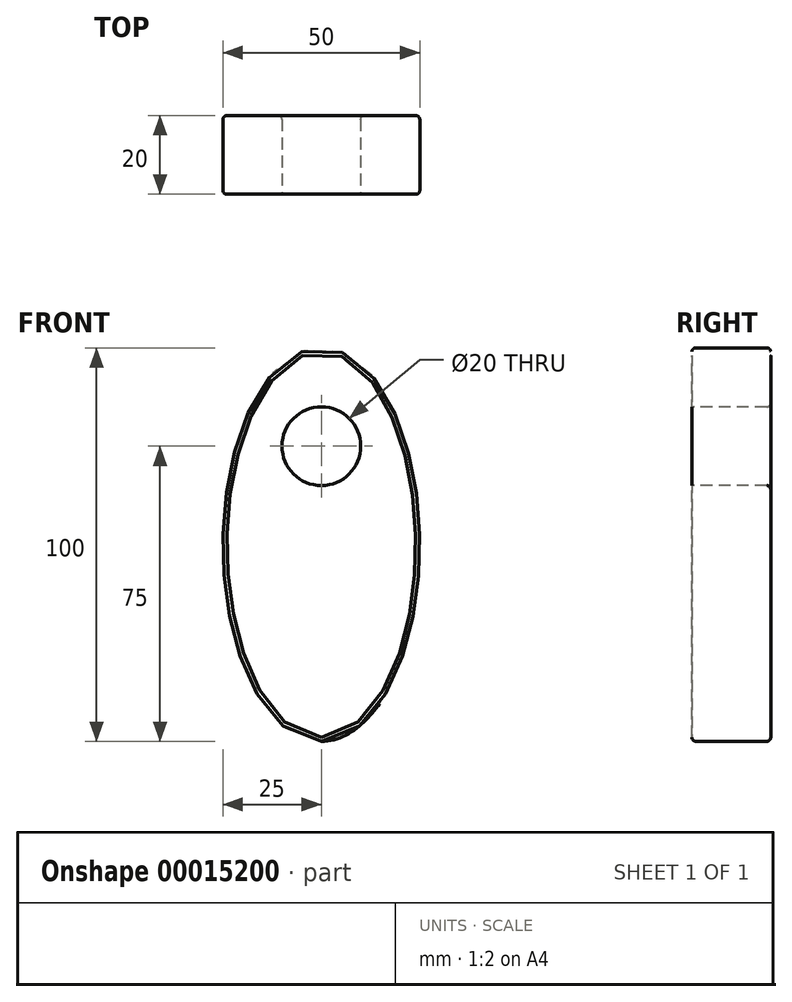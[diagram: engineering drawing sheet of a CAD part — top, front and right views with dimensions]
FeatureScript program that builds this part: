
annotation { "Feature Type Name" : "Feature", "Feature Type Description" : "" }
export const myFeature = defineFeature(function(context is Context, id is Id, definition is map)
    precondition{}
    {
        {
            var Q0;
            Q0=qCreatedBy(makeId("Front.planeOp"),FACE);
            var sketch = newSketch(context, id + "F0", { "sketchPlane" : qUnion([Q0])});
            skEllipse(sketch, "E0", {"center": v(0, 0) * mm, "majorRadius": 25 * mm, "minorRadius": 50 * mm, "majorAxis": v(-1, 0)});
            skLineSegment(sketch, "E1", {"start": v(-17.82, 16.94) * mm, "end": v(20.96, 16.94) * mm, "construction": true});
            skSolve(sketch);
        }
        {
            var Q0;
            Q0 = qSketchRegion(id + "F0", true);
            extrude(context, id + "F1", {"entities" : qUnion([Q0]), "depth" : 20 * mm});
        }
        {
            var Q0;
            Q0=makeQuery(id+"F1.opExtrude","CAP_FACE",FACE,{"disambiguationData":[OSD([sQuery(id+"F0.wireOp",EDGE,"E0")])],"isStart":false});
            var sketch = newSketch(context, id + "F2", { "sketchPlane" : qUnion([Q0])});
            skSolve(sketch);
        }
        {
            var Q0;
            Q0=makeQuery(id+"F2.imprint","IMPRINT",FACE,{"disambiguationData":[TD([[makeQuery(id+"F2.imprint","IMPRINT",EDGE,{"derivedFrom":makeQuery(id+"F1.opExtrude","CAP_EDGE",EDGE,{"disambiguationData":[OSD([sQuery(id+"F0.wireOp",EDGE,"E0")])],"isStart":false})}),1.0]])]});
            var sketch = newSketch(context, id + "F3", { "sketchPlane" : qUnion([Q0])});
            skCircle(sketch, "E2", {"center": v(0, 25) * mm, "radius": 10 * mm});
            skSolve(sketch);
        }
        {
            var Q0;
            Q0=makeQuery(id+"F3.imprint","IMPRINT",FACE,{"disambiguationData":[TD([[makeQuery(id+"F3.imprint","IMPRINT",EDGE,{"derivedFrom":sQuery(id+"F3.wireOp",EDGE,"E2")}),1.0]])]});
            extrude(context, id + "F4", {"entities" : qUnion([Q0]), "operationType" : NewBodyOperationType.REMOVE, "endBound" : BoundingType.THROUGH_ALL, "oppositeDirection" : true, "depth" : 25 * mm});
        }
        {
            var Q0;
            Q0=makeQuery(id+"F1.opExtrude","CAP_EDGE",EDGE,{"disambiguationData":[OSD([sQuery(id+"F0.wireOp",EDGE,"E0")])],"isStart":false});
            var Q1;
            Q1=makeQuery(id+"F1.opExtrude","SWEPT_FACE",FACE,{"disambiguationData":[OSD([sQuery(id+"F0.wireOp",EDGE,"E0")])]});
            var Q2;
            Q2=makeQuery(id+"F4.boolean.opBoolean","COPY",EDGE,{"derivedFrom":makeQuery(id+"F4.opExtrude","CAP_EDGE",EDGE,{"disambiguationData":[OSD([sQuery(id+"F3.wireOp",EDGE,"E2")])],"isStart":true})});
            var Q3;
            Q3=makeQuery(id+"F4.boolean.opBoolean","INTERSECT",EDGE,{"derivedFrom":[makeQuery(id+"F1.opExtrude","CAP_FACE",FACE,{"disambiguationData":[OSD([sQuery(id+"F0.wireOp",EDGE,"E0")])],"isStart":true}),makeQuery(id+"F4.opExtrude","SWEPT_FACE",FACE,{"disambiguationData":[OSD([sQuery(id+"F3.wireOp",EDGE,"E2")])]})]});
            fillet(context, id + "F5", {"entities" : qUnion([Q0, Q1, Q2, Q3]), "radius" : 1 * mm, "tangentPropagation" : true, "allowEdgeOverflow" : false});
        }
    });
